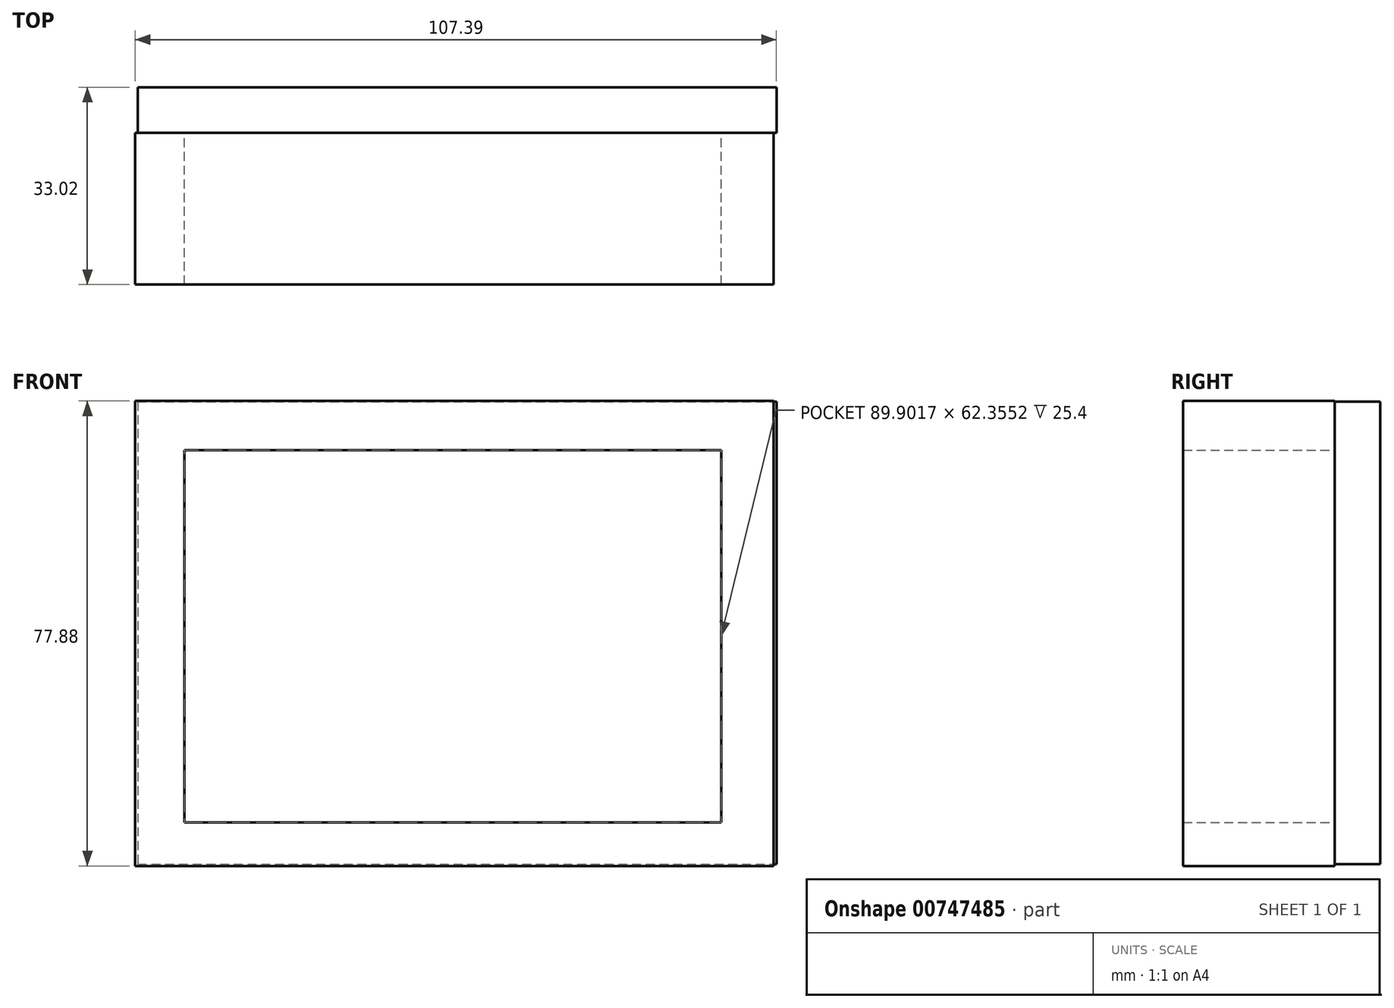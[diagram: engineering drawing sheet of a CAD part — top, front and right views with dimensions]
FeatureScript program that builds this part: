
annotation { "Feature Type Name" : "Feature", "Feature Type Description" : "" }
export const myFeature = defineFeature(function(context is Context, id is Id, definition is map)
    precondition{}
    {
        {
            var Q0;
            Q0=qCreatedBy(makeId("Front.planeOp"),FACE);
            var sketch = newSketch(context, id + "F0", { "sketchPlane" : qUnion([Q0])});
            skLineSegment(sketch, "E0.bottom", {"start": v(-52.71, 40.07) * mm, "end": v(54.22, 40.07) * mm});
            skLineSegment(sketch, "E0.top", {"start": v(-52.71, -37.81) * mm, "end": v(54.22, -37.81) * mm});
            skLineSegment(sketch, "E0.left", {"start": v(-52.71, 40.07) * mm, "end": v(-52.71, -37.81) * mm});
            skLineSegment(sketch, "E0.right", {"start": v(54.22, 40.07) * mm, "end": v(54.22, -37.81) * mm});
            skLineSegment(sketch, "E1.bottom", {"start": v(-44.45, 31.8) * mm, "end": v(45.45, 31.8) * mm});
            skLineSegment(sketch, "E1.top", {"start": v(-44.45, -30.55) * mm, "end": v(45.45, -30.55) * mm});
            skLineSegment(sketch, "E1.left", {"start": v(-44.45, 31.8) * mm, "end": v(-44.45, -30.55) * mm});
            skLineSegment(sketch, "E1.right", {"start": v(45.45, 31.8) * mm, "end": v(45.45, -30.55) * mm});
            skLineSegment(sketch, "E2.bottom", {"start": v(59.63, 40.6) * mm, "end": v(166.56, 40.6) * mm});
            skLineSegment(sketch, "E2.top", {"start": v(59.63, -37.29) * mm, "end": v(166.56, -37.29) * mm});
            skLineSegment(sketch, "E2.left", {"start": v(59.63, 40.6) * mm, "end": v(59.63, -37.29) * mm});
            skLineSegment(sketch, "E2.right", {"start": v(166.56, 40.6) * mm, "end": v(166.56, -37.29) * mm});
            skSolve(sketch);
        }
        {
            var Q0;
            Q0=makeQuery(id+"F0.imprint","IMPRINT",FACE,{"disambiguationData":[TD([[makeQuery(id+"F0.imprint","IMPRINT",EDGE,{"derivedFrom":sQuery(id+"F0.wireOp",EDGE,"E0.bottom")}),-1.0]])]});
            extrude(context, id + "F1", {"entities" : qUnion([Q0]), "depth" : 25.4 * mm, "offsetDistance" : 25.4 * mm});
        }
        {
            var Q0;
            Q0=qCreatedBy(makeId("Front.planeOp"),FACE);
            var sketch = newSketch(context, id + "F2", { "sketchPlane" : qUnion([Q0])});
            skLineSegment(sketch, "E3.bottom", {"start": v(-52.3, 39.95) * mm, "end": v(54.68, 39.95) * mm});
            skLineSegment(sketch, "E3.top", {"start": v(-52.3, -37.54) * mm, "end": v(54.68, -37.54) * mm});
            skLineSegment(sketch, "E3.left", {"start": v(-52.3, 39.95) * mm, "end": v(-52.3, -37.54) * mm});
            skLineSegment(sketch, "E3.right", {"start": v(54.68, 39.95) * mm, "end": v(54.68, -37.54) * mm});
            skSolve(sketch);
        }
        {
            var Q0;
            Q0=makeQuery(id+"F2.imprint","IMPRINT",FACE,{"disambiguationData":[TD([[makeQuery(id+"F2.imprint","IMPRINT",EDGE,{"derivedFrom":sQuery(id+"F2.wireOp",EDGE,"E3.bottom")}),-1.0]])]});
            extrude(context, id + "F3", {"entities" : qUnion([Q0]), "operationType" : NewBodyOperationType.ADD, "depth" : -7.62 * mm, "offsetDistance" : 25.4 * mm});
        }
    });
